# Revit family: Building-Materials_Waterproofing&Membranes_EMAC_NOVOMEMBRANA-EPDM
name_source: partatom
category: Generic Models
revit_build: Autodesk Revit 2015 (Build: 20140606_1530(x64)
units: mm (PartAtom-declared; Revit-internal decimal feet)

## types (4) — shared parameters
Edition number = 1
Manufacturer = EMAC
Model = NOVOMEMBRANA EPDM
Product Guid = 541b65cd-4d6f-41af-ba12-ab0ee81a66a3
Product Material = Finish_Emac_Aluminum-Anodized-Matt-Black-10
Product data url = https://www.bimobject.com

## per-type parameters (varying)
| type | Arc Height | Description | Joint Length | R | Width | Width Control | a | c | d | h | s |
| MEMEST140 | 7 mm  [stored 0.0229659 ft] | NOVOMEMBRANA EPDM hasta 40mm | 20 mm  [stored 0.0656168 ft] | 11 mm | 140 mm  [stored 0.459318 ft] | 140 mm  [stored 0.459318 ft] | 139.97° | 20 mm  [stored 0.0656168 ft] | 4 mm  [stored 0.0131234 ft] | 7 mm  [stored 0.0229659 ft] | 26 mm |
| MEMEST170 | 10 mm  [stored 0.0328084 ft] | NOVOMEMBRANA EPDM hasta 60mm | 40 mm  [stored 0.131234 ft] | 25 mm  [stored 0.082021 ft] | 170 mm  [stored 0.557743 ft] | 170 mm  [stored 0.557743 ft] | 106.26° | 40 mm  [stored 0.131234 ft] | 15 mm  [stored 0.0492126 ft] | 10 mm  [stored 0.0328084 ft] | 46 mm |
| MEMEST200 | 17 mm | NOVOMEMBRANA EPDM hasta 80mm | 50 mm  [stored 0.164042 ft] | 27 mm | 200 mm  [stored 0.656168 ft] | 200 mm  [stored 0.656168 ft] | 135.41° | 50 mm  [stored 0.164042 ft] | 10 mm  [stored 0.0328084 ft] | 17 mm | 64 mm |
| MEMEST260 | 17 mm | NOVOMEMBRANA EPDM hasta 120mm | 60 mm  [stored 0.19685 ft] | 35 mm | 260 mm  [stored 0.853018 ft] | 260 mm  [stored 0.853018 ft] | 116.82° | 60 mm  [stored 0.19685 ft] | 18 mm | 17 mm | 72 mm |

note: [stored X ft] marks values corroborated as IEEE doubles in the binary element streams (Revit-internal decimal feet)

## geometry (parser evidence)
native form markers: Sweep x3
no freeform markers — native parametric forms only
